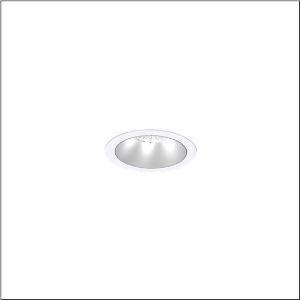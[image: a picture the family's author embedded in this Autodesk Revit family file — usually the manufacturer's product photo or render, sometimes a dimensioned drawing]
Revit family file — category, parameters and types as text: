
# Revit family: lunis_21_m_51db19tc91c
name_source: partatom
category: Lighting Fixtures
units: mm (PartAtom-declared; Revit-internal decimal feet)

## family parameters
Cut with Voids When Loaded = No
Host = Face
Light Source = No
Part Type = Normal
Room Calculation Point = No
Round Connector Dimension = Use Diameter
Shared = No

## types (1)
- --- (1 x LED, 3750 lm, 26 W, 4000K)
    Apparent Load = 26 VA
    CIE Flux Codes = 95 100 100 100 100
    Color Rendering = 80
    Color Temperature = 4000K
    Default Elevation = 1800 mm
    Description = Lunis 21,  M, downlight, light control with lens, of PMMA, anti glare with reflector, of aluminium, matt, light emission: direct distribution, LED rated luminous flux: 1.730lm, light colour: 8tw, with terminal, 5-pole, mains connection: 220..240V, AC/DC, 0/50..60Hz, housing, round, of diecast aluminium, traffic white (RAL 9016), diameter: 115mm, clamping range: 1..40mm, protection rating (complete): IP20, protection rating (on room side): IP54, insulation class (complete): insulation class II (safety insulation), certification: CE, impact resistance: IK03, packaging unit: 1 piece
    Height = 0 mm  [stored 0 ft]
    Lamp = 1 x LED
    Lamp Light Flux = 3750 lm
    Lamp Power = 26 W
    Lamp count = 1
    Length = 115 mm
    Luminous efficacy = 144 lm/W
    Manufacturer = Siteco
    ModVariant = No
    Model = 51DB19TC91C
    Mounting Place = Ceiling
    Mounting Type = Recessed
    Number of Poles = 1
    OnlyDefault = Yes
    Power Factor = 1
    Product Name = Lunis 21 M
    Product group = downlight
    ProductGroupID = 400
    Protection Class = Protection class II
    Protection Degree = IP 20
    RLX_Detail_Level = 1
    RLX_Emergency_Light_Flux = 0 lm
    RLX_Emergency_Type = 0
    RLX_Emergency_Type_DB = No
    RlxData = <blob elided: 11297 chars, md5=094c1e47>
    Socket = socket
    Standby Power = 0 W
    System Light Flux = 3750 lm
    System Power = 26 W
    Type Comments = individual setting: colour temperature 4000K, luminous flux: 100 % | (ON | ON | OFF | OFF) | 700 mA
    Type Image = l_1290856.jpg
    URL = http://relux.com
    VarID = @adj_017541
    Voltage = 0 V
    Weight = 0.00 kg
    Width = 0 mm  [stored 0 ft]

note: [stored X ft] marks values corroborated as IEEE doubles in the binary element streams (Revit-internal decimal feet)

## geometry (parser evidence)
native form markers: Sweep x7
no freeform markers — native parametric forms only
